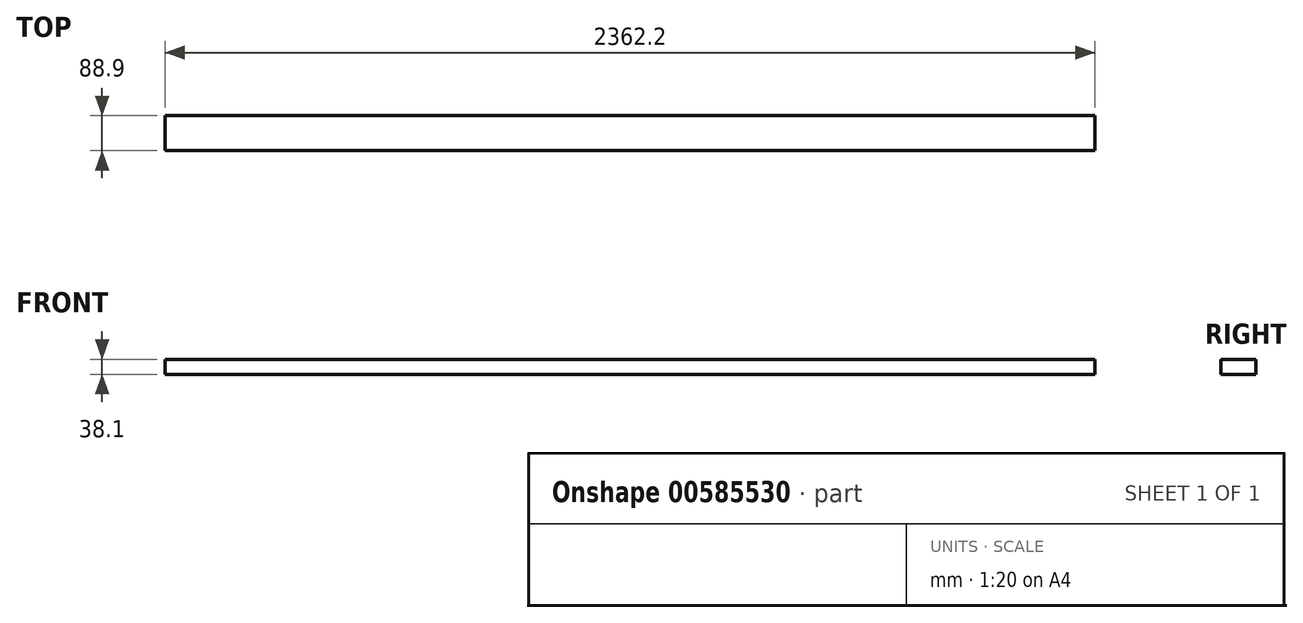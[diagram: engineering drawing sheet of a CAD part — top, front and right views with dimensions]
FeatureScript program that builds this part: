
annotation { "Feature Type Name" : "Feature", "Feature Type Description" : "" }
export const myFeature = defineFeature(function(context is Context, id is Id, definition is map)
    precondition{}
    {
        {
            var Q0;
            Q0=qCreatedBy(makeId("Top.planeOp"),FACE);
            var sketch = newSketch(context, id + "F0", { "sketchPlane" : qUnion([Q0])});
            skLineSegment(sketch, "E0.bottom", {"start": v(1181.1, -44.45) * mm, "end": v(-1181.1, -44.45) * mm});
            skLineSegment(sketch, "E0.top", {"start": v(1181.1, 44.45) * mm, "end": v(-1181.1, 44.45) * mm});
            skLineSegment(sketch, "E0.left", {"start": v(1181.1, -44.45) * mm, "end": v(1181.1, 44.45) * mm});
            skLineSegment(sketch, "E0.right", {"start": v(-1181.1, -44.45) * mm, "end": v(-1181.1, 44.45) * mm});
            skPoint(sketch, "E0.middle", {"position": v(0, 0) * mm});
            skSolve(sketch);
        }
        {
            var Q0;
            Q0 = qSketchRegion(id + "F0", true);
            extrude(context, id + "F1", {"entities" : qUnion([Q0]), "endBound" : BoundingType.SYMMETRIC, "depth" : 38.1 * mm, "offsetDistance" : 25.4 * mm});
        }
    });
